# Revit family: Overhead_Door-CHI_Overhead_Doors-Sectional_Sandwich
name_source: partatom
category: Specialty Equipment
units: mm (PartAtom-declared; Revit-internal decimal feet)

## family parameters
Always vertical = Yes
Cut with Voids When Loaded = No
Enable Cutting in Views = No
Host = Wall
Maintain Annotation Orientation = No
OmniClass Number = 23.30.10.21
OmniClass Title = Special Function Doors
Part Type = Normal
Room Calculation Point = No
Round Connector Dimension = Use Diameter
Shared = No

## types (1)
- Not a Type - Load by Type Catalog
    Air Infiltration = 0.15
    Appearance = Micro-grooved
    Assembly Code = B2030410
    C Appeance = 2
    C Door Bottom Offset = 0' - 0 3/8"
    C Side Rail Radius = 1' - 3"
    Certified Windload = No
    Closing Speed = Contact Manufacturer for More Information
    Constraints = 1
    Construction Type = Micro-grooved insulated sandwich garage bay doors
    DASMA Thermal Verification Program = Yes
    Default Elevation = 0' - 0"
    Description = Micro-Grooved Insulated Sandwich Garage Bay Doors
    Fire Rating = Contact Manufacturer for More Information
    IECC Compliant = Yes
    Impact = No
    Keynote = 08 30 00
    Load Classification = Other
    Manufacturer = C.H.I. Overhead Doors
    Manufacturer Fax Number = 800-738-5006
    Model = 3206
    Number of Phases = 1
    Number of Poles = 1
    Opening Speed = Contact Manufacturer for More Information
    Operation = Insulated sandwich garage bay doors
    Panel Finish = Metal - Powder Coat - C.H.I Overhead Doors - White
    Product Documentation Link = https://cdn2.hubspot.net
    Product Page URL = https://www.chiohd.com
    R-Value = 13.68
    STC = Contact Manufacturer for More Information
    Section Thickness = 0' - 1 1/2"
    Steel Gauge = 28
    Thickness = 0' - 1 1/2"
    U Factor = 0.19
    URL = https://www.chiohd.com
    Version = 2021-v1.a
    Voltage = 115 V

## geometry (parser evidence)
native form markers: Sweep x43
no freeform markers — native parametric forms only
